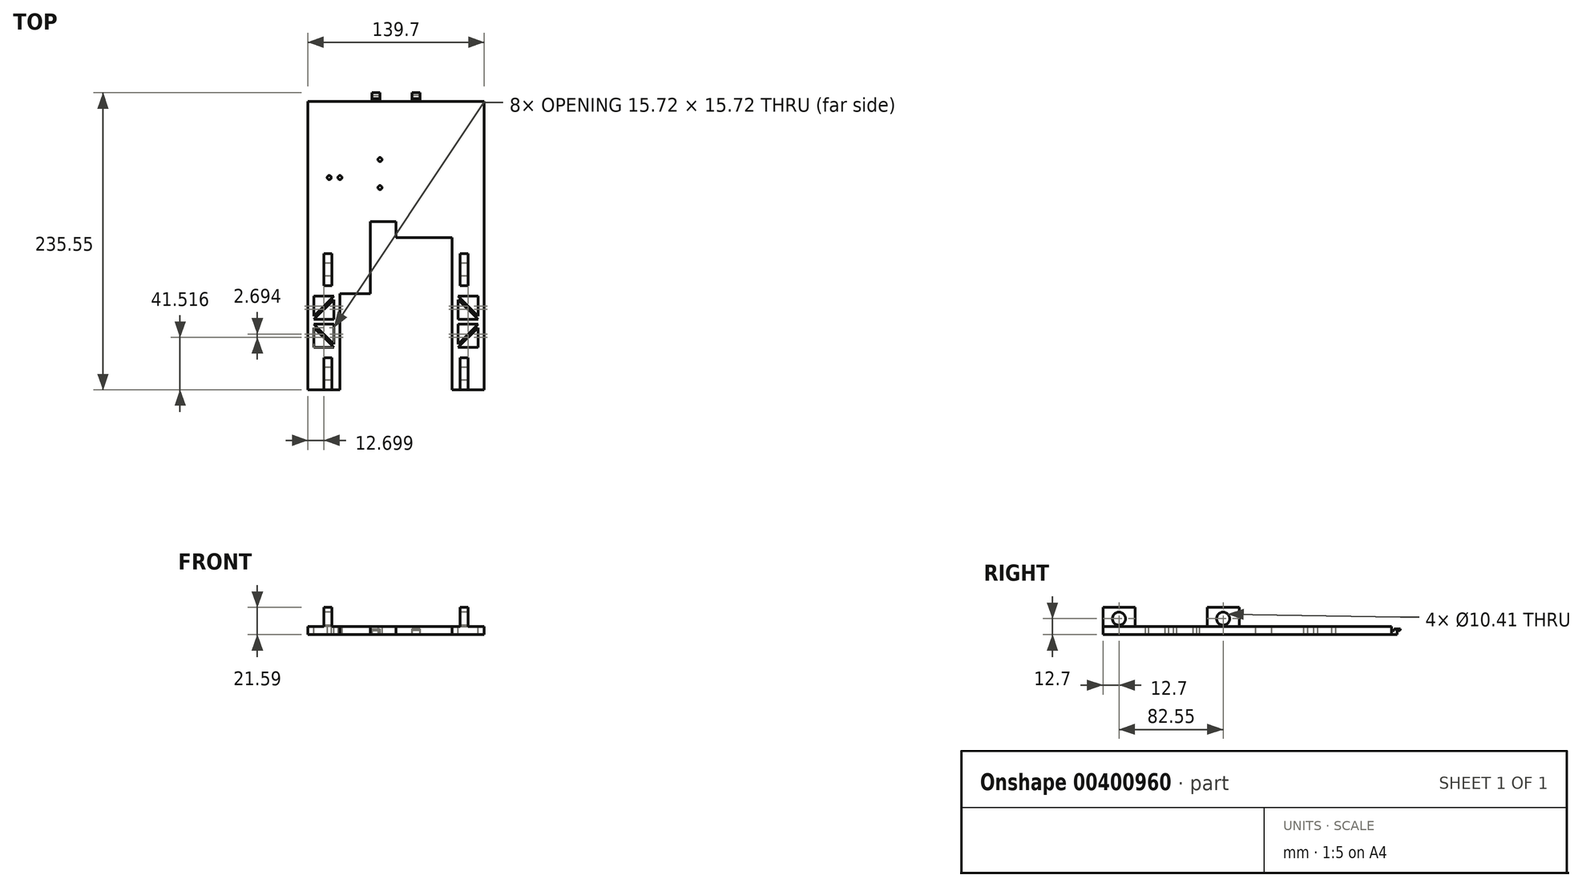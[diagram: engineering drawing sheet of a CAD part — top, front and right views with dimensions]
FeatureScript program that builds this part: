
annotation { "Feature Type Name" : "Feature", "Feature Type Description" : "" }
export const myFeature = defineFeature(function(context is Context, id is Id, definition is map)
    precondition{}
    {
        {
            var Q0;
            Q0=qCreatedBy(makeId("Top.planeOp"),FACE);
            var sketch = newSketch(context, id + "F0", { "sketchPlane" : qUnion([Q0])});
            skLineSegment(sketch, "E0.bottom", {"start": v(-69.85, 114.3) * mm, "end": v(69.85, 114.3) * mm});
            skLineSegment(sketch, "E0.top", {"start": v(-69.85, -114.3) * mm, "end": v(69.85, -114.3) * mm});
            skLineSegment(sketch, "E0.left", {"start": v(-69.85, 114.3) * mm, "end": v(-69.85, -114.3) * mm});
            skLineSegment(sketch, "E0.right", {"start": v(69.85, 114.3) * mm, "end": v(69.85, -114.3) * mm});
            skPoint(sketch, "E0.middle", {"position": v(0, 0) * mm});
            skLineSegment(sketch, "E1.bottom", {"start": v(-44.45, -114.3) * mm, "end": v(44.45, -114.3) * mm});
            skLineSegment(sketch, "E1.top", {"start": v(-44.45, -38.1) * mm, "end": v(44.45, -38.1) * mm});
            skLineSegment(sketch, "E1.left", {"start": v(-44.45, -114.3) * mm, "end": v(-44.45, -38.1) * mm});
            skLineSegment(sketch, "E1.right", {"start": v(44.45, -114.3) * mm, "end": v(44.45, -38.1) * mm});
            skLineSegment(sketch, "E2.bottom", {"start": v(44.45, -38.1) * mm, "end": v(0, -38.1) * mm});
            skLineSegment(sketch, "E2.top", {"start": v(44.45, 6.35) * mm, "end": v(0, 6.35) * mm});
            skLineSegment(sketch, "E2.left", {"start": v(44.45, -38.1) * mm, "end": v(44.45, 6.35) * mm});
            skLineSegment(sketch, "E2.right", {"start": v(0, -38.1) * mm, "end": v(0, 6.35) * mm});
            skLineSegment(sketch, "E3.bottom", {"start": v(0, -38.1) * mm, "end": v(-20.32, -38.1) * mm});
            skLineSegment(sketch, "E3.top", {"start": v(0, 19.05) * mm, "end": v(-20.32, 19.05) * mm});
            skLineSegment(sketch, "E3.left", {"start": v(0, -38.1) * mm, "end": v(0, 19.05) * mm});
            skLineSegment(sketch, "E3.right", {"start": v(-20.32, -38.1) * mm, "end": v(-20.32, 19.05) * mm});
            skLineSegment(sketch, "E4.left", {"start": v(-44.45, -114.3) * mm, "end": v(-44.45, -107.95) * mm});
            skLineSegment(sketch, "E4.right", {"start": v(44.45, -95.25) * mm, "end": v(44.45, -88.9) * mm});
            skPoint(sketch, "E5", {"position": v(-12.7, 68.26) * mm});
            skPoint(sketch, "E6", {"position": v(-12.7, 46.04) * mm});
            skCircle(sketch, "E7", {"center": v(-12.7, 46.04) * mm, "radius": 1.59 * mm});
            skCircle(sketch, "E8", {"center": v(-12.7, 68.26) * mm, "radius": 1.59 * mm});
            skPoint(sketch, "E9", {"position": v(-44.45, 53.98) * mm});
            skPoint(sketch, "E10", {"position": v(-52.92, 53.98) * mm});
            skCircle(sketch, "E11", {"center": v(-52.92, 53.98) * mm, "radius": 1.59 * mm});
            skCircle(sketch, "E12", {"center": v(-44.45, 53.98) * mm, "radius": 1.59 * mm});
            skSolve(sketch);
        }
        {
            var Q0;
            Q0=makeQuery(id+"F0.imprint","IMPRINT",FACE,{"disambiguationData":[TD([[makeQuery(id+"F0.imprint","IMPRINT",EDGE,{"derivedFrom":sQuery(id+"F0.wireOp",EDGE,"E0.bottom")}),-1.0]])]});
            extrude(context, id + "F1", {"entities" : qUnion([Q0]), "depth" : 6.35 * mm});
        }
        {
            var Q0;
            Q0=makeQuery(id+"F1.opExtrude","CAP_FACE",FACE,{"disambiguationData":[OSD([sQuery(id+"F0.wireOp",EDGE,"E0.bottom"),sQuery(id+"F0.wireOp",EDGE,"E0.top"),sQuery(id+"F0.wireOp",EDGE,"E0.left"),sQuery(id+"F0.wireOp",EDGE,"E0.right"),sQuery(id+"F0.wireOp",EDGE,"E1.top"),sQuery(id+"F0.wireOp",EDGE,"E1.left"),sQuery(id+"F0.wireOp",EDGE,"E1.right")])],"isStart":false});
            var sketch = newSketch(context, id + "F2", { "sketchPlane" : qUnion([Q0])});
            skLineSegment(sketch, "E13.bottom", {"start": v(-57.15, -88.9) * mm, "end": v(-50.8, -88.9) * mm});
            skLineSegment(sketch, "E13.top", {"start": v(-57.15, -114.3) * mm, "end": v(-50.8, -114.3) * mm});
            skLineSegment(sketch, "E13.left", {"start": v(-57.15, -88.9) * mm, "end": v(-57.15, -114.3) * mm});
            skLineSegment(sketch, "E13.right", {"start": v(-50.8, -88.9) * mm, "end": v(-50.8, -114.3) * mm});
            skLineSegment(sketch, "E14.bottom", {"start": v(50.8, -88.9) * mm, "end": v(57.15, -88.9) * mm});
            skLineSegment(sketch, "E14.top", {"start": v(50.8, -114.3) * mm, "end": v(57.15, -114.3) * mm});
            skLineSegment(sketch, "E14.left", {"start": v(50.8, -88.9) * mm, "end": v(50.8, -114.3) * mm});
            skLineSegment(sketch, "E14.right", {"start": v(57.15, -88.9) * mm, "end": v(57.15, -114.3) * mm});
            skLineSegment(sketch, "E15.bottom", {"start": v(-57.15, -6.35) * mm, "end": v(-50.8, -6.35) * mm});
            skLineSegment(sketch, "E15.top", {"start": v(-57.15, -31.75) * mm, "end": v(-50.8, -31.75) * mm});
            skLineSegment(sketch, "E15.left", {"start": v(-57.15, -6.35) * mm, "end": v(-57.15, -31.75) * mm});
            skLineSegment(sketch, "E15.right", {"start": v(-50.8, -6.35) * mm, "end": v(-50.8, -31.75) * mm});
            skPoint(sketch, "E16.oppositeSnap0", {"position": v(57.15, -101.6) * mm});
            skLineSegment(sketch, "E16.bottom", {"start": v(50.8, -31.75) * mm, "end": v(57.15, -31.75) * mm});
            skLineSegment(sketch, "E16.top", {"start": v(50.8, -6.35) * mm, "end": v(57.15, -6.35) * mm});
            skLineSegment(sketch, "E16.left", {"start": v(50.8, -31.75) * mm, "end": v(50.8, -6.35) * mm});
            skLineSegment(sketch, "E16.right", {"start": v(57.15, -31.75) * mm, "end": v(57.15, -6.35) * mm});
            skPoint(sketch, "E17", {"position": v(57.15, -19.05) * mm});
            skPoint(sketch, "E18", {"position": v(-57.15, -19.05) * mm});
            skPoint(sketch, "E19", {"position": v(-57.15, -101.6) * mm});
            skSolve(sketch);
        }
        {
            var Q0;
            Q0=qSketchRegion(id+"F2",true);
            extrude(context, id + "F3", {"entities" : qUnion([Q0]), "operationType" : NewBodyOperationType.ADD, "depth" : 15.24 * mm});
        }
        {
            var Q0;
            Q0=makeQuery(id+"F3.opExtrude","SWEPT_FACE",FACE,{"disambiguationData":[OSD([sQuery(id+"F2.wireOp",EDGE,"E14.right")])]});
            var sketch = newSketch(context, id + "F4", { "sketchPlane" : qUnion([Q0])});
            skPoint(sketch, "E20", {"position": v(-101.6, 12.7) * mm});
            skPoint(sketch, "E21", {"position": v(-19.05, 12.7) * mm});
            skSolve(sketch);
        }
        {
            var Q0;
            Q0=sQuery(id+"F4.wireOp",VERTEX,"E20");
            var Q1;
            Q1=sQuery(id+"F4.wireOp",VERTEX,"E21");
            var Q2;
            Q2=makeQuery(id+"F1.opExtrude","SWEPT_BODY",BODY,{"disambiguationData":[OSD([sQuery(id+"F0.wireOp",EDGE,"E0.bottom"),sQuery(id+"F0.wireOp",EDGE,"E0.top"),sQuery(id+"F0.wireOp",EDGE,"E0.left"),sQuery(id+"F0.wireOp",EDGE,"E0.right"),sQuery(id+"F0.wireOp",EDGE,"E1.top"),sQuery(id+"F0.wireOp",EDGE,"E1.left"),sQuery(id+"F0.wireOp",EDGE,"E1.right")])]});
            hole(context, id + "F5", {"style" : HoleStyle.SIMPLE, "endStyle" : HoleEndStyle.THROUGH, "holeDiameter" : 10.4 * mm, "isTappedThrough" : true, "tappedDepth" : 12.7 * mm, "tapClearance" : 3, "startFromSketch" : true, "locations" : qUnion([Q0, Q1]), "scope" : qUnion([Q2])});
        }
        {
            var Q0;
            Q0=makeQuery(id+"F1.opExtrude","SWEPT_FACE",FACE,{"disambiguationData":[OSD([sQuery(id+"F0.wireOp",EDGE,"E0.right")])]});
            var Q1;
            Q1=makeQuery(id+"F1.opExtrude","SWEPT_FACE",FACE,{"disambiguationData":[OSD([sQuery(id+"F0.wireOp",EDGE,"E0.left")])]});
            cPlane(context, id + "F6", {"entities" : qUnion([Q0, Q1]), "cplaneType" : CPlaneType.MID_PLANE, "offset" : 25.4 * mm, "width" : 152.4 * mm, "height" : 152.4 * mm});
        }
        {
            var Q0;
            Q0=qCreatedBy(id+"F6.planeOp",FACE);
            cPlane(context, id + "F7", {"entities" : qUnion([Q0]), "cplaneType" : CPlaneType.OFFSET, "offset" : 12.7 * mm, "width" : 152.4 * mm, "height" : 152.4 * mm});
        }
        {
            var Q0;
            Q0=qCreatedBy(id+"F7.planeOp",FACE);
            var sketch = newSketch(context, id + "F8", { "sketchPlane" : qUnion([Q0])});
            skLineSegment(sketch, "E22", {"start": v(118.94, 4.64) * mm, "end": v(118.94, 3.37) * mm});
            skLineSegment(sketch, "E23", {"start": v(116.62, 3.18) * mm, "end": v(114.3, 3.18) * mm});
            skLineSegment(sketch, "E24.MirrorCS", {"start": v(114.3, 0) * mm, "end": v(118.94, 0) * mm});
            skLineSegment(sketch, "E25.MirrorCS", {"start": v(114.3, 3.18) * mm, "end": v(114.3, 0) * mm});
            skLineSegment(sketch, "E26.MirrorCS", {"start": v(118.94, 0) * mm, "end": v(118.94, 3.37) * mm});
            skLineSegment(sketch, "E27.MirrorCS", {"start": v(121.25, 4.64) * mm, "end": v(116.62, 4.64) * mm});
            skLineSegment(sketch, "E28.MirrorCS", {"start": v(116.62, 4.64) * mm, "end": v(116.62, 3.18) * mm});
            skLineSegment(sketch, "E29.MirrorCS", {"start": v(121.25, 3.37) * mm, "end": v(121.25, 4.64) * mm});
            skLineSegment(sketch, "E30.MirrorCS", {"start": v(118.94, 3.37) * mm, "end": v(121.25, 3.37) * mm});
            skPoint(sketch, "E31.orphan", {"position": v(118.94, 6.35) * mm});
            skPoint(sketch, "E32.end.orphan", {"position": v(114.3, 6.35) * mm});
            skPoint(sketch, "E33.start.orphan", {"position": v(118.94, 2.98) * mm});
            skPoint(sketch, "E34.start.orphan", {"position": v(121.25, 2.98) * mm});
            skPoint(sketch, "E35.orphan", {"position": v(121.25, 1.71) * mm});
            skPoint(sketch, "E36.start.orphan", {"position": v(116.62, 1.71) * mm});
            skSolve(sketch);
        }
        {
            var Q0;
            Q0=qSketchRegion(id+"F8",true);
            extrude(context, id + "F9", {"entities" : qUnion([Q0]), "operationType" : NewBodyOperationType.ADD, "depth" : 6.35 * mm});
        }
        {
            var Q0;
            Q0=qCreatedBy(id+"F6.planeOp",FACE);
            cPlane(context, id + "F10", {"entities" : qUnion([Q0]), "cplaneType" : CPlaneType.OFFSET, "offset" : 12.7 * mm, "oppositeDirection" : true, "width" : 152.4 * mm, "height" : 152.4 * mm});
        }
        {
            var Q0;
            Q0=qCreatedBy(id+"F10.planeOp",FACE);
            var sketch = newSketch(context, id + "F11", { "sketchPlane" : qUnion([Q0])});
            skLineSegment(sketch, "E37", {"start": v(118.94, 4.64) * mm, "end": v(118.94, 3.37) * mm});
            skLineSegment(sketch, "E38", {"start": v(116.62, 3.18) * mm, "end": v(114.3, 3.18) * mm});
            skLineSegment(sketch, "E39.MirrorCS", {"start": v(114.3, 0) * mm, "end": v(118.94, 0) * mm});
            skLineSegment(sketch, "E40.MirrorCS", {"start": v(114.3, 3.18) * mm, "end": v(114.3, 0) * mm});
            skLineSegment(sketch, "E41.MirrorCS", {"start": v(118.94, 0) * mm, "end": v(118.94, 3.37) * mm});
            skLineSegment(sketch, "E42.MirrorCS", {"start": v(121.25, 4.64) * mm, "end": v(116.62, 4.64) * mm});
            skLineSegment(sketch, "E43.MirrorCS", {"start": v(116.62, 4.64) * mm, "end": v(116.62, 3.18) * mm});
            skLineSegment(sketch, "E44.MirrorCS", {"start": v(121.25, 3.37) * mm, "end": v(121.25, 4.64) * mm});
            skLineSegment(sketch, "E45.MirrorCS", {"start": v(118.94, 3.37) * mm, "end": v(121.25, 3.37) * mm});
            skPoint(sketch, "E46.orphan", {"position": v(118.94, 6.35) * mm});
            skPoint(sketch, "E47.end.orphan", {"position": v(114.3, 6.35) * mm});
            skPoint(sketch, "E48.start.orphan", {"position": v(118.94, 2.98) * mm});
            skPoint(sketch, "E49.start.orphan", {"position": v(121.25, 2.98) * mm});
            skPoint(sketch, "E50.orphan", {"position": v(121.25, 1.71) * mm});
            skPoint(sketch, "E51.start.orphan", {"position": v(116.62, 1.71) * mm});
            skSolve(sketch);
        }
        {
            var Q0;
            Q0=qSketchRegion(id+"F11",true);
            extrude(context, id + "F12", {"entities" : qUnion([Q0]), "operationType" : NewBodyOperationType.ADD, "oppositeDirection" : true, "depth" : 6.35 * mm});
        }
        {
            var Q0;
            Q0=makeQuery(id+"F9.opExtrude","SWEPT_EDGE",EDGE,{"disambiguationData":[OSD([sQuery(id+"F8.wireOp",EDGE,"E29.MirrorCS"),sQuery(id+"F8.wireOp",EDGE,"E30.MirrorCS")])]});
            var Q1;
            Q1=makeQuery(id+"F12.opExtrude","SWEPT_EDGE",EDGE,{"disambiguationData":[OSD([sQuery(id+"F11.wireOp",EDGE,"E44.MirrorCS"),sQuery(id+"F11.wireOp",EDGE,"E45.MirrorCS")])]});
            var Q2;
            Q2=makeQuery(id+"F12.opExtrude","SWEPT_EDGE",EDGE,{"disambiguationData":[OSD([sQuery(id+"F11.wireOp",EDGE,"E42.MirrorCS"),sQuery(id+"F11.wireOp",EDGE,"E43.MirrorCS")])]});
            var Q3;
            Q3=makeQuery(id+"F9.opExtrude","SWEPT_EDGE",EDGE,{"disambiguationData":[OSD([sQuery(id+"F8.wireOp",EDGE,"E27.MirrorCS"),sQuery(id+"F8.wireOp",EDGE,"E28.MirrorCS")])]});
            fillet(context, id + "F13", {"entities" : qUnion([Q0, Q1, Q2, Q3]), "radius" : 0.5 * mm, "tangentPropagation" : true, "allowEdgeOverflow" : false});
        }
        {
            var Q0;
            Q0=makeQuery(id+"F2.imprint","IMPRINT",FACE,{"disambiguationData":[TD([[makeQuery(id+"F2.imprint","IMPRINT",EDGE,{"derivedFrom":sQuery(id+"F2.wireOp",EDGE,"E13.bottom")}),1.0]])]});
            var sketch = newSketch(context, id + "F14", { "sketchPlane" : qUnion([Q0])});
            skLineSegment(sketch, "E52.0.0", {"start": v(44.45, 6.35) * mm, "end": v(44.45, -114.3) * mm});
            skLineSegment(sketch, "E52.0.1", {"start": v(44.45, -114.3) * mm, "end": v(69.85, -114.3) * mm});
            skLineSegment(sketch, "E52.0.2", {"start": v(69.85, -114.3) * mm, "end": v(69.85, 114.3) * mm});
            skLineSegment(sketch, "E52.0.3", {"start": v(69.85, 114.3) * mm, "end": v(-69.85, 114.3) * mm});
            skLineSegment(sketch, "E52.0.4", {"start": v(-69.85, 114.3) * mm, "end": v(-69.85, -114.3) * mm});
            skLineSegment(sketch, "E52.0.5", {"start": v(-69.85, -114.3) * mm, "end": v(-57.15, -114.3) * mm});
            skLineSegment(sketch, "E52.0.6", {"start": v(-44.45, -114.3) * mm, "end": v(-44.45, -38.1) * mm});
            skLineSegment(sketch, "E52.0.7", {"start": v(-44.45, -38.1) * mm, "end": v(-20.32, -38.1) * mm});
            skLineSegment(sketch, "E52.0.8", {"start": v(-20.32, -38.1) * mm, "end": v(-20.32, 19.05) * mm});
            skLineSegment(sketch, "E52.0.9", {"start": v(-20.32, 19.05) * mm, "end": v(0, 19.05) * mm});
            skLineSegment(sketch, "E52.0.10", {"start": v(0, 19.05) * mm, "end": v(0, 6.35) * mm});
            skLineSegment(sketch, "E52.0.11", {"start": v(0, 6.35) * mm, "end": v(44.45, 6.35) * mm});
            skLineSegment(sketch, "E53", {"start": v(-44.45, -38.1) * mm, "end": v(-69.85, -38.1) * mm});
            skLineSegment(sketch, "E54", {"start": v(-65.01, -40) * mm, "end": v(-49.3, -40) * mm});
            skLineSegment(sketch, "E55", {"start": v(-49.3, -40) * mm, "end": v(-65.01, -55.73) * mm});
            skLineSegment(sketch, "E56", {"start": v(-65.01, -55.73) * mm, "end": v(-65.01, -40) * mm});
            skLineSegment(sketch, "E57", {"start": v(-49.3, -42.7) * mm, "end": v(-65.01, -58.42) * mm});
            skLineSegment(sketch, "E58", {"start": v(-65.01, -58.42) * mm, "end": v(-49.3, -58.42) * mm});
            skLineSegment(sketch, "E59", {"start": v(-49.3, -58.42) * mm, "end": v(-49.3, -42.7) * mm});
            skLineSegment(sketch, "E60", {"start": v(-69.85, -60.32) * mm, "end": v(-44.45, -60.32) * mm, "construction": true});
            skLineSegment(sketch, "E61.MirrorCS", {"start": v(-65.01, -62.23) * mm, "end": v(-49.3, -62.23) * mm});
            skLineSegment(sketch, "E62.MirrorCS", {"start": v(-65.01, -80.64) * mm, "end": v(-49.3, -80.64) * mm});
            skLineSegment(sketch, "E63.MirrorCS", {"start": v(-49.3, -80.64) * mm, "end": v(-65.01, -64.92) * mm});
            skLineSegment(sketch, "E64.MirrorCS", {"start": v(-65.01, -64.92) * mm, "end": v(-65.01, -80.64) * mm});
            skLineSegment(sketch, "E65.MirrorCS", {"start": v(-49.3, -77.95) * mm, "end": v(-65.01, -62.23) * mm});
            skLineSegment(sketch, "E66.MirrorCS", {"start": v(-49.3, -62.23) * mm, "end": v(-49.3, -77.95) * mm});
            skLineSegment(sketch, "E67.MirrorCS", {"start": v(65.01, -55.73) * mm, "end": v(65.01, -40) * mm});
            skLineSegment(sketch, "E68.MirrorCS", {"start": v(65.01, -40) * mm, "end": v(49.3, -40) * mm});
            skLineSegment(sketch, "E69.MirrorCS", {"start": v(49.3, -40) * mm, "end": v(65.01, -55.73) * mm});
            skLineSegment(sketch, "E70.MirrorCS", {"start": v(49.3, -42.7) * mm, "end": v(65.01, -58.42) * mm});
            skLineSegment(sketch, "E71.MirrorCS", {"start": v(49.3, -58.42) * mm, "end": v(49.3, -42.7) * mm});
            skLineSegment(sketch, "E72.MirrorCS", {"start": v(65.01, -58.42) * mm, "end": v(49.3, -58.42) * mm});
            skLineSegment(sketch, "E73.MirrorCS", {"start": v(65.01, -62.23) * mm, "end": v(49.3, -62.23) * mm});
            skLineSegment(sketch, "E74.MirrorCS", {"start": v(49.3, -77.95) * mm, "end": v(65.01, -62.23) * mm});
            skLineSegment(sketch, "E75.MirrorCS", {"start": v(49.3, -62.23) * mm, "end": v(49.3, -77.95) * mm});
            skLineSegment(sketch, "E76.MirrorCS", {"start": v(49.3, -80.64) * mm, "end": v(65.01, -64.92) * mm});
            skLineSegment(sketch, "E77.MirrorCS", {"start": v(65.01, -64.92) * mm, "end": v(65.01, -80.64) * mm});
            skLineSegment(sketch, "E78.MirrorCS", {"start": v(65.01, -80.64) * mm, "end": v(49.3, -80.64) * mm});
            skSolve(sketch);
        }
        {
            var Q0;
            Q0=makeQuery(id+"F14.imprint","IMPRINT",FACE,{"disambiguationData":[TD([[makeQuery(id+"F14.imprint","IMPRINT",EDGE,{"derivedFrom":sQuery(id+"F14.wireOp",EDGE,"E54")}),-1.0]])]});
            var Q1;
            Q1=makeQuery(id+"F14.imprint","IMPRINT",FACE,{"disambiguationData":[TD([[makeQuery(id+"F14.imprint","IMPRINT",EDGE,{"derivedFrom":sQuery(id+"F14.wireOp",EDGE,"E57")}),1.0]])]});
            var Q2;
            Q2=makeQuery(id+"F14.imprint","IMPRINT",FACE,{"disambiguationData":[TD([[makeQuery(id+"F14.imprint","IMPRINT",EDGE,{"derivedFrom":sQuery(id+"F14.wireOp",EDGE,"E61.MirrorCS")}),-1.0]])]});
            var Q3;
            Q3=makeQuery(id+"F14.imprint","IMPRINT",FACE,{"disambiguationData":[TD([[makeQuery(id+"F14.imprint","IMPRINT",EDGE,{"derivedFrom":sQuery(id+"F14.wireOp",EDGE,"E62.MirrorCS")}),1.0]])]});
            var Q4;
            Q4=makeQuery(id+"F14.imprint","IMPRINT",FACE,{"disambiguationData":[TD([[makeQuery(id+"F14.imprint","IMPRINT",EDGE,{"derivedFrom":sQuery(id+"F14.wireOp",EDGE,"E76.MirrorCS")}),-1.0]])]});
            var Q5;
            Q5=makeQuery(id+"F14.imprint","IMPRINT",FACE,{"disambiguationData":[TD([[makeQuery(id+"F14.imprint","IMPRINT",EDGE,{"derivedFrom":sQuery(id+"F14.wireOp",EDGE,"E73.MirrorCS")}),1.0]])]});
            var Q6;
            Q6=makeQuery(id+"F14.imprint","IMPRINT",FACE,{"disambiguationData":[TD([[makeQuery(id+"F14.imprint","IMPRINT",EDGE,{"derivedFrom":sQuery(id+"F14.wireOp",EDGE,"E70.MirrorCS")}),-1.0]])]});
            var Q7;
            Q7=makeQuery(id+"F14.imprint","IMPRINT",FACE,{"disambiguationData":[TD([[makeQuery(id+"F14.imprint","IMPRINT",EDGE,{"derivedFrom":sQuery(id+"F14.wireOp",EDGE,"E67.MirrorCS")}),1.0]])]});
            extrude(context, id + "F15", {"entities" : qUnion([Q0, Q1, Q2, Q3, Q4, Q5, Q6, Q7]), "operationType" : NewBodyOperationType.REMOVE, "oppositeDirection" : true, "depth" : 25.4 * mm});
        }
    });
